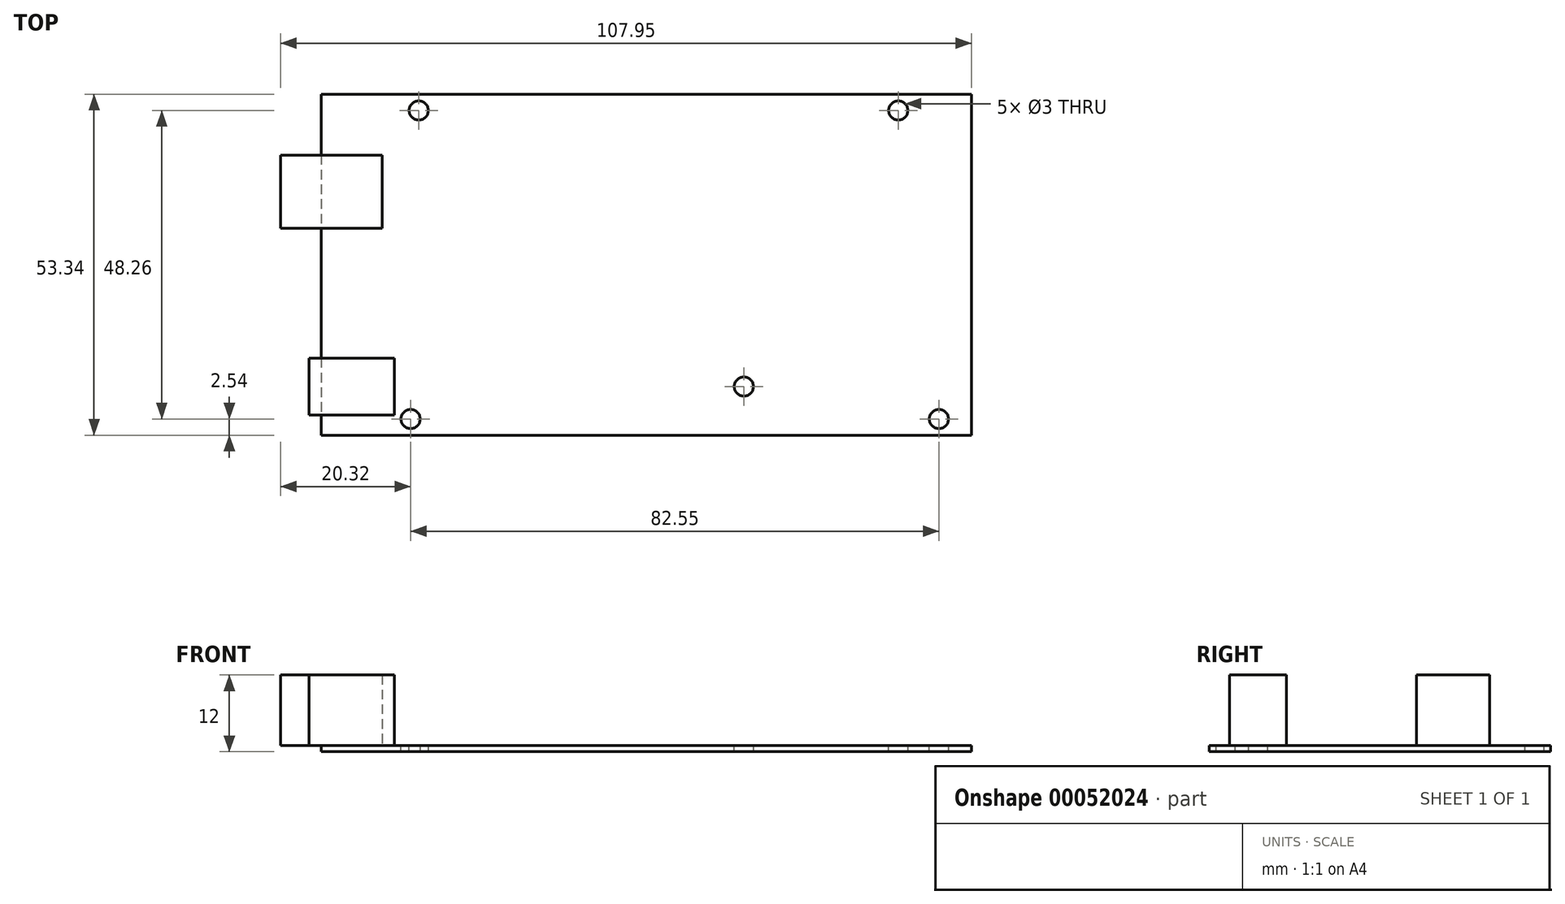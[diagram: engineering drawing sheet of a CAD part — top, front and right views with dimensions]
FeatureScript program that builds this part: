
annotation { "Feature Type Name" : "Feature", "Feature Type Description" : "" }
export const myFeature = defineFeature(function(context is Context, id is Id, definition is map)
    precondition{}
    {
        {
            var Q0;
            Q0=qCreatedBy(makeId("Top.planeOp"),FACE);
            var sketch = newSketch(context, id + "F0", { "sketchPlane" : qUnion([Q0])});
            skLineSegment(sketch, "E0.bottom", {"start": v(-50.8, 26.67) * mm, "end": v(50.8, 26.67) * mm});
            skLineSegment(sketch, "E0.top", {"start": v(-50.8, -26.67) * mm, "end": v(50.8, -26.67) * mm});
            skLineSegment(sketch, "E0.left", {"start": v(-50.8, 26.67) * mm, "end": v(-50.8, -26.67) * mm});
            skLineSegment(sketch, "E0.right", {"start": v(50.8, 26.67) * mm, "end": v(50.8, -26.67) * mm});
            skLineSegment(sketch, "E1", {"start": v(-50.8, 26.67) * mm, "end": v(50.8, -26.67) * mm, "construction": true});
            skPoint(sketch, "E2", {"position": v(0, 0) * mm});
            skSolve(sketch);
        }
        {
            var Q0;
            Q0=makeQuery(id+"F0.imprint","IMPRINT",FACE,{"disambiguationData":[TD([[makeQuery(id+"F0.imprint","IMPRINT",EDGE,{"derivedFrom":sQuery(id+"F0.wireOp",EDGE,"E0.bottom")}),-1.0]])]});
            extrude(context, id + "F1", {"entities" : qUnion([Q0]), "depth" : 1 * mm});
        }
        {
            var Q0;
            Q0=makeQuery(id+"F1.opExtrude","CAP_FACE",FACE,{"disambiguationData":[OSD([sQuery(id+"F0.wireOp",EDGE,"E0.bottom"),sQuery(id+"F0.wireOp",EDGE,"E0.top"),sQuery(id+"F0.wireOp",EDGE,"E0.left"),sQuery(id+"F0.wireOp",EDGE,"E0.right")])],"isStart":false});
            var sketch = newSketch(context, id + "F2", { "sketchPlane" : qUnion([Q0])});
            skPoint(sketch, "E3", {"position": v(-36.83, -24.13) * mm});
            skPoint(sketch, "E4", {"position": v(-35.56, 24.13) * mm});
            skPoint(sketch, "E5", {"position": v(15.24, -19.05) * mm});
            skPoint(sketch, "E6", {"position": v(45.72, -24.13) * mm});
            skPoint(sketch, "E7", {"position": v(39.37, 24.13) * mm});
            skSolve(sketch);
        }
        {
            var Q0;
            Q0=sQuery(id+"F2.wireOp",VERTEX,"E4");
            var Q1;
            Q1=sQuery(id+"F2.wireOp",VERTEX,"E7");
            var Q2;
            Q2=sQuery(id+"F2.wireOp",VERTEX,"E6");
            var Q3;
            Q3=sQuery(id+"F2.wireOp",VERTEX,"E5");
            var Q4;
            Q4=sQuery(id+"F2.wireOp",VERTEX,"E3");
            var Q5;
            Q5=makeQuery(id+"F1.opExtrude","SWEPT_BODY",BODY,{"disambiguationData":[OSD([sQuery(id+"F0.wireOp",EDGE,"E0.bottom"),sQuery(id+"F0.wireOp",EDGE,"E0.top"),sQuery(id+"F0.wireOp",EDGE,"E0.left"),sQuery(id+"F0.wireOp",EDGE,"E0.right")])]});
            hole(context, id + "F3", {"style" : HoleStyle.SIMPLE, "endStyle" : HoleEndStyle.THROUGH, "holeDiameter" : 3 * mm, "locations" : qUnion([Q0, Q1, Q2, Q3, Q4]), "scope" : qUnion([Q5]), "isTappedThrough" : true});
        }
        {
            var Q0;
            Q0=makeQuery(id+"F1.opExtrude","CAP_FACE",FACE,{"disambiguationData":[OSD([sQuery(id+"F0.wireOp",EDGE,"E0.bottom"),sQuery(id+"F0.wireOp",EDGE,"E0.top"),sQuery(id+"F0.wireOp",EDGE,"E0.left"),sQuery(id+"F0.wireOp",EDGE,"E0.right")])],"isStart":false});
            var sketch = newSketch(context, id + "F4", { "sketchPlane" : qUnion([Q0])});
            skLineSegment(sketch, "E8.bottom", {"start": v(-57.15, 17.14) * mm, "end": v(-41.28, 17.14) * mm});
            skLineSegment(sketch, "E8.top", {"start": v(-57.15, 5.72) * mm, "end": v(-41.28, 5.72) * mm});
            skLineSegment(sketch, "E8.left", {"start": v(-57.15, 17.14) * mm, "end": v(-57.15, 5.71) * mm});
            skLineSegment(sketch, "E8.right", {"start": v(-41.28, 17.14) * mm, "end": v(-41.28, 5.72) * mm});
            skLineSegment(sketch, "E9.bottom", {"start": v(-52.7, -14.6) * mm, "end": v(-39.37, -14.6) * mm});
            skLineSegment(sketch, "E9.top", {"start": v(-52.7, -23.5) * mm, "end": v(-39.37, -23.5) * mm});
            skLineSegment(sketch, "E9.left", {"start": v(-52.7, -14.6) * mm, "end": v(-52.7, -23.5) * mm});
            skLineSegment(sketch, "E9.right", {"start": v(-39.37, -14.6) * mm, "end": v(-39.37, -23.5) * mm});
            skSolve(sketch);
        }
        {
            var Q0;
            {var subQ0=sQuery(id+"F4.wireOp",EDGE,"E8.right");Q0=makeQuery(id+"F4.imprint","IMPRINT",FACE,{"disambiguationData":[TD([[makeQuery(id+"F4.imprint","IMPRINT",EDGE,{"derivedFrom":subQ0}),-1.0]])]});}
            var Q1;
            {var subQ0=sQuery(id+"F4.wireOp",EDGE,"E8.left");Q1=makeQuery(id+"F4.imprint","IMPRINT",FACE,{"disambiguationData":[TD([[makeQuery(id+"F4.imprint","IMPRINT",EDGE,{"derivedFrom":subQ0}),1.0]])]});}
            var Q2;
            {var subQ0=sQuery(id+"F4.wireOp",EDGE,"E9.right");Q2=makeQuery(id+"F4.imprint","IMPRINT",FACE,{"disambiguationData":[TD([[makeQuery(id+"F4.imprint","IMPRINT",EDGE,{"derivedFrom":subQ0}),-1.0]])]});}
            var Q3;
            {var subQ0=sQuery(id+"F4.wireOp",EDGE,"E9.left");Q3=makeQuery(id+"F4.imprint","IMPRINT",FACE,{"disambiguationData":[TD([[makeQuery(id+"F4.imprint","IMPRINT",EDGE,{"derivedFrom":subQ0}),1.0]])]});}
            extrude(context, id + "F5", {"entities" : qUnion([Q0, Q1, Q2, Q3]), "operationType" : NewBodyOperationType.ADD, "depth" : 11 * mm});
        }
    });
